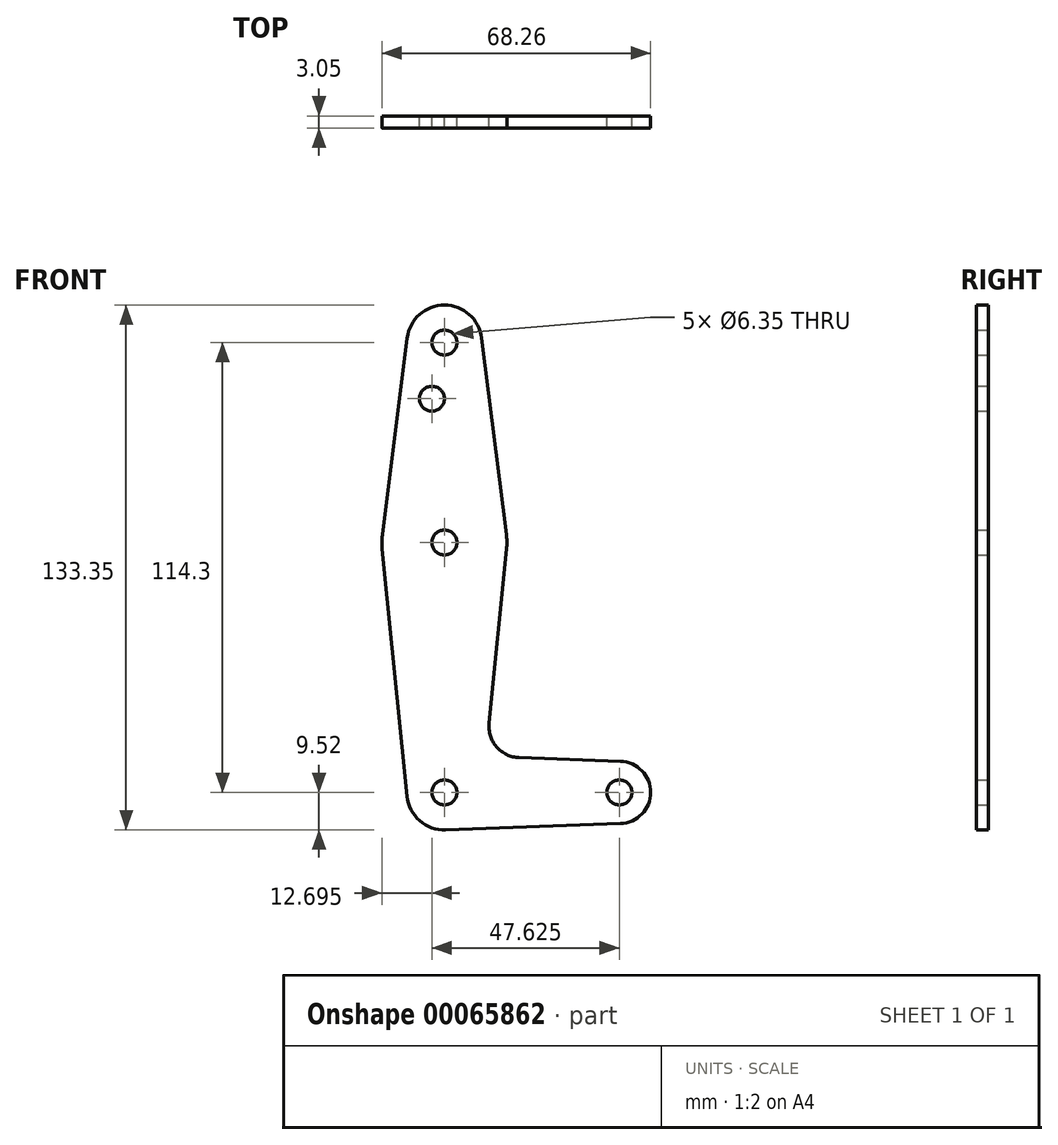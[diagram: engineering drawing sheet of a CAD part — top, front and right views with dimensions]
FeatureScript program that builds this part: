
annotation { "Feature Type Name" : "Feature", "Feature Type Description" : "" }
export const myFeature = defineFeature(function(context is Context, id is Id, definition is map)
    precondition{}
    {
        {
            var Q0;
            Q0=qCreatedBy(makeId("Front.planeOp"),FACE);
            var sketch = newSketch(context, id + "F0", { "sketchPlane" : qUnion([Q0])});
            skLineSegment(sketch, "E0", {"start": v(0, 114.3) * mm, "end": v(0, 63.5) * mm, "construction": true});
            skLineSegment(sketch, "E1", {"start": v(0, 63.5) * mm, "end": v(0, 0) * mm, "construction": true});
            skLineSegment(sketch, "E2", {"start": v(0, 0) * mm, "end": v(44.45, 0) * mm, "construction": true});
            skCircle(sketch, "E3", {"center": v(0, 114.3) * mm, "radius": 9.53 * mm});
            skCircle(sketch, "E4", {"center": v(0, 63.5) * mm, "radius": 15.88 * mm});
            skCircle(sketch, "E5", {"center": v(0, 0) * mm, "radius": 9.53 * mm});
            skCircle(sketch, "E6", {"center": v(44.45, 0) * mm, "radius": 7.94 * mm});
            skLineSegment(sketch, "E7", {"start": v(-9.45, 115.5) * mm, "end": v(-15.75, 65.48) * mm});
            skLineSegment(sketch, "E8", {"start": v(9.45, 115.5) * mm, "end": v(15.75, 65.48) * mm});
            skLineSegment(sketch, "E9", {"start": v(15.8, 61.91) * mm, "end": v(11.34, 17.6) * mm});
            skLineSegment(sketch, "E10", {"start": v(44.73, 7.93) * mm, "end": v(18.97, 8.85) * mm});
            skLineSegment(sketch, "E11", {"start": v(44.73, -7.93) * mm, "end": v(0.34, -9.52) * mm});
            skLineSegment(sketch, "E12", {"start": v(-15.8, 61.91) * mm, "end": v(-9.48, -0.95) * mm});
            skCircle(sketch, "E13", {"center": v(0, 114.3) * mm, "radius": 3.18 * mm});
            skCircle(sketch, "E14", {"center": v(0, 63.5) * mm, "radius": 3.18 * mm});
            skCircle(sketch, "E15", {"center": v(0, 0) * mm, "radius": 3.18 * mm});
            skCircle(sketch, "E16", {"center": v(44.45, 0) * mm, "radius": 3.18 * mm});
            skCircle(sketch, "E17", {"center": v(-3.18, 100.03) * mm, "radius": 3.18 * mm});
            skArc(sketch, "E18.filletArc", {"start": v(11.34, 17.6) * mm, "mid": v(13.26, 11.57) * mm, "end": v(18.97, 8.85) * mm});
            skSolve(sketch);
        }
        {
            var Q0;
            Q0 = qSketchRegion(id + "F0", true);
            extrude(context, id + "F1", {"entities" : qUnion([Q0]), "depth" : 3.05 * mm});
        }
    });
